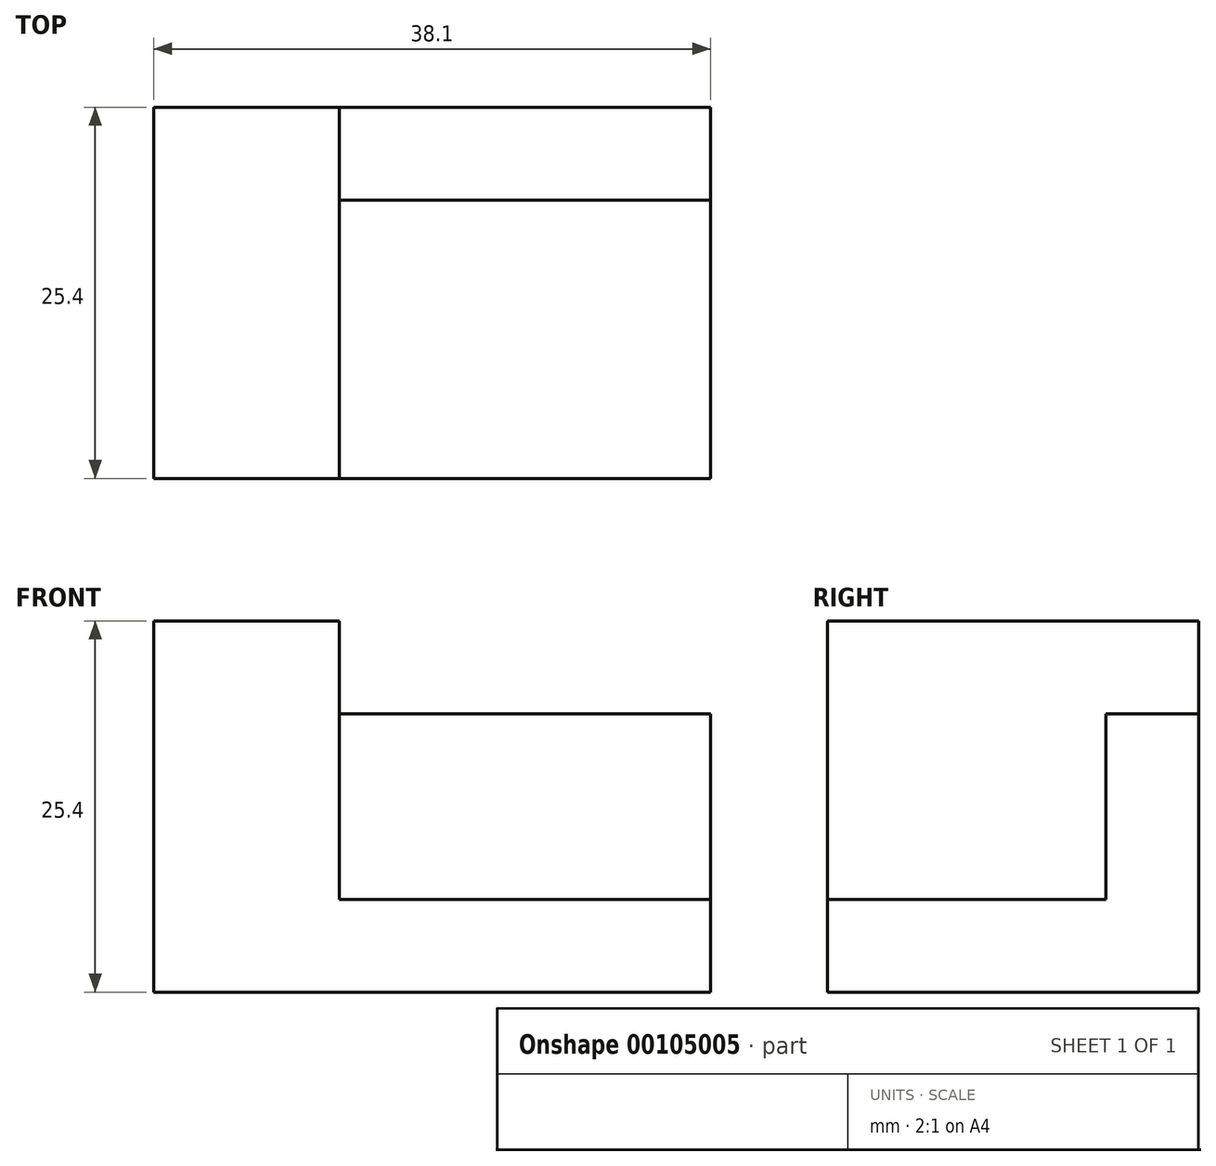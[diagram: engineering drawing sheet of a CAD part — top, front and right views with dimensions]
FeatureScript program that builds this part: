
annotation { "Feature Type Name" : "Feature", "Feature Type Description" : "" }
export const myFeature = defineFeature(function(context is Context, id is Id, definition is map)
    precondition{}
    {
        {
            var Q0;
            Q0=qCreatedBy(makeId("Front.planeOp"),FACE);
            var sketch = newSketch(context, id + "F0", { "sketchPlane" : qUnion([Q0])});
            skLineSegment(sketch, "E0", {"start": v(0, 0) * mm, "end": v(0, 25.4) * mm});
            skLineSegment(sketch, "E1", {"start": v(0, 25.4) * mm, "end": v(12.7, 25.4) * mm});
            skLineSegment(sketch, "E2", {"start": v(12.7, 25.4) * mm, "end": v(12.7, 6.35) * mm});
            skLineSegment(sketch, "E3", {"start": v(12.7, 6.35) * mm, "end": v(38.1, 6.35) * mm});
            skLineSegment(sketch, "E4", {"start": v(38.1, 6.35) * mm, "end": v(38.1, 0) * mm});
            skLineSegment(sketch, "E5", {"start": v(38.1, 0) * mm, "end": v(0, 0) * mm});
            skSolve(sketch);
        }
        {
            var Q0;
            Q0=qCreatedBy(makeId("Right.planeOp"),FACE);
            var sketch = newSketch(context, id + "F1", { "sketchPlane" : qUnion([Q0])});
            skLineSegment(sketch, "E6.bottom", {"start": v(0, 0) * mm, "end": v(25.4, 0) * mm});
            skLineSegment(sketch, "E6.top", {"start": v(0, 25.4) * mm, "end": v(25.4, 25.4) * mm});
            skLineSegment(sketch, "E6.left", {"start": v(0, 0) * mm, "end": v(0, 25.4) * mm});
            skLineSegment(sketch, "E6.right", {"start": v(25.4, 0) * mm, "end": v(25.4, 25.4) * mm});
            skLineSegment(sketch, "E7", {"start": v(0, 6.35) * mm, "end": v(19.05, 6.35) * mm});
            skLineSegment(sketch, "E8", {"start": v(19.05, 6.35) * mm, "end": v(19.05, 19.05) * mm});
            skLineSegment(sketch, "E9", {"start": v(19.05, 19.05) * mm, "end": v(25.4, 19.05) * mm});
            skSolve(sketch);
        }
        {
            var Q0;
            {var subQ2=sQuery(id+"F1.wireOp",EDGE,"E6.bottom");Q0=makeQuery(id+"F1.imprint","IMPRINT",FACE,{"disambiguationData":[TD([[makeQuery(id+"F1.imprint","IMPRINT",EDGE,{"derivedFrom":subQ2}),1.0]])]});}
            extrude(context, id + "F2", {"entities" : qUnion([Q0]), "depth" : 38.1 * mm});
        }
        {
            var Q0;
            Q0=makeQuery(id+"F0.imprint","IMPRINT",FACE,{"disambiguationData":[TD([[makeQuery(id+"F0.imprint","IMPRINT",EDGE,{"derivedFrom":sQuery(id+"F0.wireOp",EDGE,"E0")}),-1.0]])]});
            extrude(context, id + "F3", {"entities" : qUnion([Q0]), "operationType" : NewBodyOperationType.ADD, "oppositeDirection" : true, "depth" : 25.4 * mm});
        }
    });
